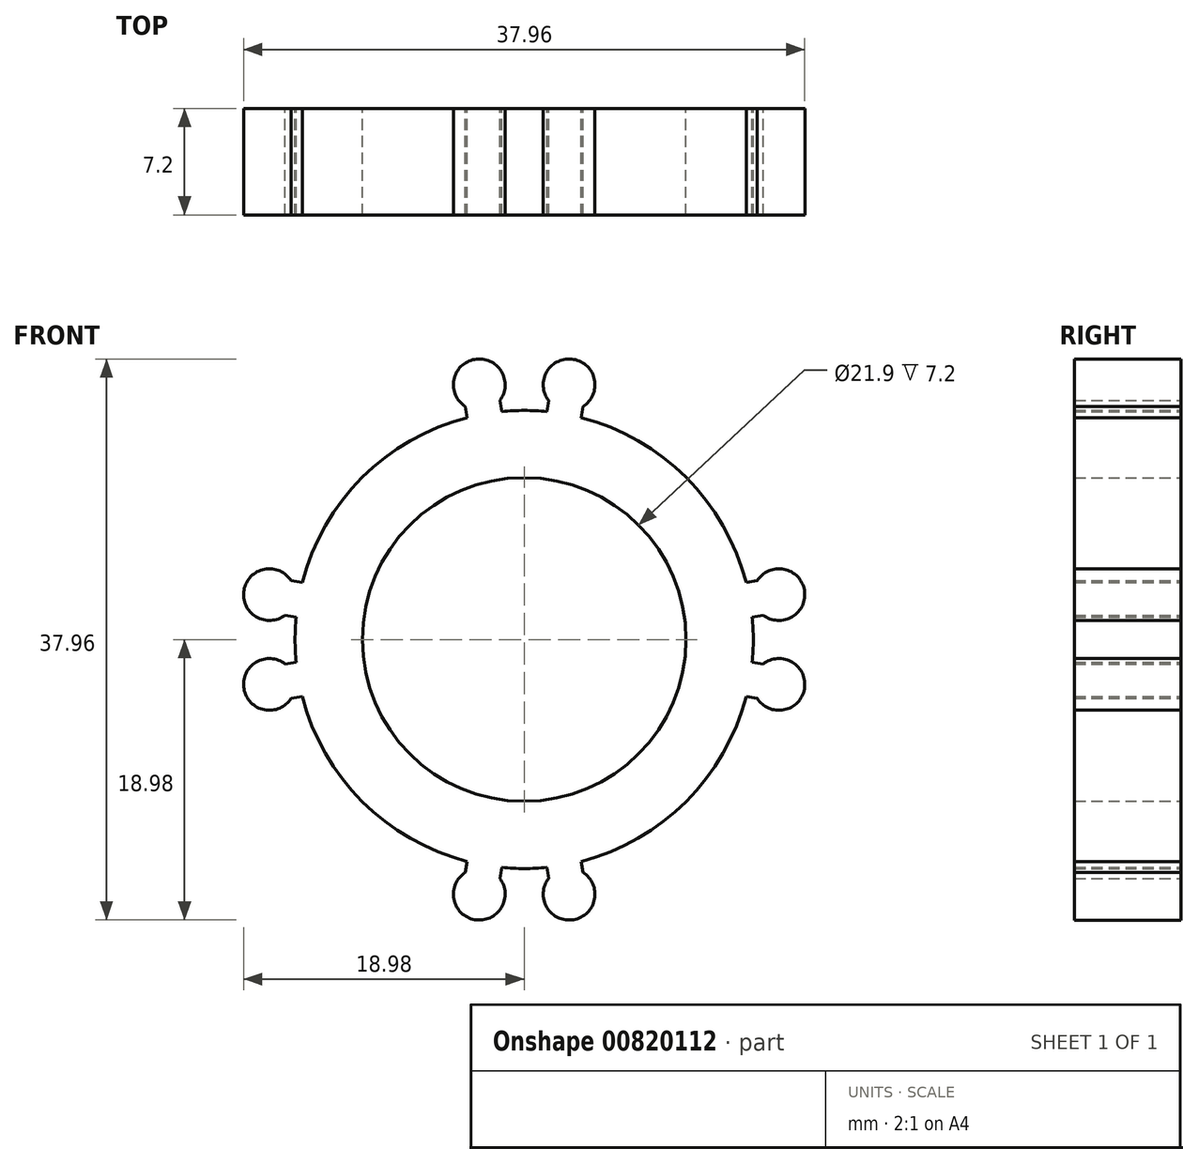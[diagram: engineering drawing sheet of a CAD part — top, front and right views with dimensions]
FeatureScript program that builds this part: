
annotation { "Feature Type Name" : "Feature", "Feature Type Description" : "" }
export const myFeature = defineFeature(function(context is Context, id is Id, definition is map)
    precondition{}
    {
        {
            var Q0;
            Q0=qCreatedBy(makeId("Front.planeOp"),FACE);
            var sketch = newSketch(context, id + "F0", { "sketchPlane" : qUnion([Q0])});
            skCircle(sketch, "E0", {"center": v(0, 0) * mm, "radius": 10.95 * mm});
            skArc(sketch, "E1", {"start": v(-3.85, 15.02) * mm, "mid": v(0, -15.5) * mm, "end": v(3.85, 15.02) * mm});
            skLineSegment(sketch, "E2", {"start": v(0, 0) * mm, "end": v(0, 44.16) * mm, "construction": true});
            skCircle(sketch, "E3", {"center": v(0, 0) * mm, "radius": 17.5 * mm, "construction": true});
            skArc(sketch, "E4", {"start": v(-1.65, 16.17) * mm, "mid": v(-3.34, 18.96) * mm, "end": v(-3.98, 15.76) * mm});
            skCircle(sketch, "E5", {"center": v(0, 0) * mm, "radius": 16.25 * mm, "construction": true});
            skLineSegment(sketch, "E6", {"start": v(-3.98, 15.76) * mm, "end": v(-3.85, 15.02) * mm});
            skLineSegment(sketch, "E7", {"start": v(-3.04, 17.23) * mm, "end": v(0, 0) * mm, "construction": true});
            skLineSegment(sketch, "E8.MirrorCS", {"start": v(-1.65, 16.17) * mm, "end": v(-1.52, 15.43) * mm});
            skLineSegment(sketch, "E9.MirrorCS", {"start": v(3.98, 15.76) * mm, "end": v(3.85, 15.02) * mm});
            skLineSegment(sketch, "E10.MirrorCS", {"start": v(1.65, 16.17) * mm, "end": v(1.52, 15.43) * mm});
            skArc(sketch, "E11.MirrorCS", {"start": v(1.65, 16.17) * mm, "mid": v(3.34, 18.96) * mm, "end": v(3.98, 15.76) * mm});
            skArc(sketch, "E12.trimOffspring", {"start": v(1.52, 15.43) * mm, "mid": v(0, 15.5) * mm, "end": v(-1.52, 15.43) * mm});
            skLineSegment(sketch, "E13.1.0", {"start": v(-16.17, 1.65) * mm, "end": v(-15.43, 1.52) * mm});
            skArc(sketch, "E13.1.1", {"start": v(-16.17, 1.65) * mm, "mid": v(-18.96, 3.34) * mm, "end": v(-15.76, 3.98) * mm});
            skLineSegment(sketch, "E13.1.2", {"start": v(-15.76, 3.98) * mm, "end": v(-15.02, 3.85) * mm});
            skLineSegment(sketch, "E13.1.3", {"start": v(-16.17, -1.65) * mm, "end": v(-15.43, -1.52) * mm});
            skLineSegment(sketch, "E13.1.4", {"start": v(-15.76, -3.98) * mm, "end": v(-15.02, -3.85) * mm});
            skArc(sketch, "E13.1.5", {"start": v(-16.17, -1.65) * mm, "mid": v(-18.96, -3.34) * mm, "end": v(-15.76, -3.98) * mm});
            skLineSegment(sketch, "E13.2.0", {"start": v(-1.65, -16.17) * mm, "end": v(-1.52, -15.43) * mm});
            skArc(sketch, "E13.2.1", {"start": v(-1.65, -16.17) * mm, "mid": v(-3.34, -18.96) * mm, "end": v(-3.98, -15.76) * mm});
            skLineSegment(sketch, "E13.2.2", {"start": v(-3.98, -15.76) * mm, "end": v(-3.85, -15.02) * mm});
            skLineSegment(sketch, "E13.2.3", {"start": v(1.65, -16.17) * mm, "end": v(1.52, -15.43) * mm});
            skLineSegment(sketch, "E13.2.4", {"start": v(3.98, -15.76) * mm, "end": v(3.85, -15.02) * mm});
            skArc(sketch, "E13.2.5", {"start": v(1.65, -16.17) * mm, "mid": v(3.34, -18.96) * mm, "end": v(3.98, -15.76) * mm});
            skArc(sketch, "E14.3.3.0", {"start": v(16.17, -1.65) * mm, "mid": v(18.96, -3.34) * mm, "end": v(15.76, -3.98) * mm});
            skLineSegment(sketch, "E14.7.3.0", {"start": v(15.76, -3.98) * mm, "end": v(15.02, -3.85) * mm});
            skLineSegment(sketch, "E14.10.3.0", {"start": v(16.17, 1.65) * mm, "end": v(15.43, 1.52) * mm});
            skLineSegment(sketch, "E14.13.3.0", {"start": v(15.76, 3.98) * mm, "end": v(15.02, 3.85) * mm});
            skLineSegment(sketch, "E14.15.3.0", {"start": v(16.17, -1.65) * mm, "end": v(15.43, -1.52) * mm});
            skArc(sketch, "E14.16.3.0", {"start": v(16.17, 1.65) * mm, "mid": v(18.96, 3.34) * mm, "end": v(15.76, 3.98) * mm});
            skSolve(sketch);
        }
        {
            var Q0;
            Q0 = qSketchRegion(id + "F0", true);
            extrude(context, id + "F1", {"entities" : qUnion([Q0]), "depth" : 7.2 * mm, "offsetDistance" : 25 * mm});
        }
    });
